# Revit family: CLNC15A428x65
name_source: partatom
category: Structural Connections
revit_build: Autodesk Revit 2015 (Build: 20140606_1530(x64)
units: mm (PartAtom-declared; Revit-internal decimal feet)

## types (1)
- CLNC15A428x65
    Default Elevation = 0 mm  [stored 0 ft]
    Density = 0.00 kg
    Description = Simpson Strong-Tie
    EPD = 23.20.40.11.14.17
    ETA / DoP = 0.003
    Manufacturer = Simpson Strong-Tie
    Model = CLNC15A42,8x65
    Model Disclaimer = Contact Simpson Strong-Tie Company  for more information
    Model ID = =Product type
    Name = CLNC15A42,8x65
    ObjectType = CLNC15A42,8x65
    Product Material = Stainless steel A4
    Product Type = Simpson Strong-Tie
    Reference = 75744
    Technical datasheet = https://www.strongtie.eu
    URL = www.strongtie.eu
    UniClass Number = #REF!
    UniClass Title = #REF!

note: [stored X ft] marks values corroborated as IEEE doubles in the binary element streams (Revit-internal decimal feet)

## geometry (parser evidence)
native form markers: Blend x24, Sweep x3
no freeform markers — native parametric forms only
